# Revit family: 210_CAD O Integral EX 35 VLEXD
name_source: partatom
category: Mechanical Equipment
units: mm (PartAtom-declared; Revit-internal decimal feet)

## family parameters
Always vertical = Yes
Cut with Voids When Loaded = No
Part Type = Breaks Into
Room Calculation Point = No
Round Connector Dimension = Use Diameter
Shared = No
Work Plane-Based = No

## types (1)
- CAD O Integral EX 35 VLEXD
    AA1 = 779 mm  [stored 2.55577 ft]
    AA2 = 59 mm
    AA2__ve = -59 mm
    AA3 = 779 mm  [stored 2.55577 ft]
    AA4 = 838 mm
    BB1 = 563 mm  [stored 1.84711 ft]
    CAT0 = Yes
    D = 450 mm
    HH1 = 1363 mm  [stored 4.47178 ft]
    QmdConnectorList = 221;D;231;D;241;D;251;D
    R = 225 mm  [stored 0.738189 ft]
    SPG = 436 mm  [stored 1.43045 ft]
    SPH = 1026 mm  [stored 3.36614 ft]
    SPI1 = 563 mm  [stored 1.84711 ft]
    SPI2 = 563 mm  [stored 1.84711 ft]
    SPN = 1818 mm  [stored 5.96457 ft]
    SPR = 99 mm  [stored 0.324803 ft]
    SPS = 54 mm  [stored 0.177165 ft]
    SS1 = 655 mm
    SS2 = 909 mm  [stored 2.98228 ft]
    W = 500 mm
    magiPartTypeId = 210
    magiProductCode = CAD O Integral EX 35 VLEXD
    magiProductFamilyId = CAD O Integral EX 35 VLEXD
    magiProductId = CAD O Integral EX 35 VLEXD

note: [stored X ft] marks values corroborated as IEEE doubles in the binary element streams (Revit-internal decimal feet)

## geometry (parser evidence)
native form markers: Sweep x2
no freeform markers — native parametric forms only
